# Revit family: Hager-Volta-IP30-Surface_mounted-empty-NoHosted-PL-en
name_source: partatom
category: Electrical Equipment
units: mm (PartAtom-declared; Revit-internal decimal feet)

## family parameters
Always vertical = Yes
Cut with Voids When Loaded = No
Panel Configuration = Two Columns, Circuits Across
Part Type = Panelboard
Room Calculation Point = No
Round Connector Dimension = Use Diameter
Shared = No
Work Plane-Based = Yes

## types (4) — shared parameters
Default Elevation = 1219 mm
EF000003 - Mounting method = EV000384 - Surface mounted (plaster)
EF000008 - Width = 305 mm  [stored 1.00066 ft]
EF000049 - Depth = 96 mm  [stored 0.314961 ft]
EF000116 - RAL-number = 9010
EF000118 - With mounting plate = Yes
EF001062 - EMC-version = No
EF002950 - Width in number of modular spacings = 12
EF005474 - Degree of protection (IP) = EV006410 - IP30
EF006244 - Transparent cover/door = No
EF006306 - With lock = No
EF015776 - Earthing terminal block = No
EF015777 - Neutral terminal block = No
EF015941 - Signal passing door = No
HG000002 - With door or cover = Yes
HG000003 - Range = Volta
HG000005 - Thickness = 3 mm  [stored 0.00984252 ft]
HG000006 - Flush mounted = No
HG000009 - Double swing door = No
HG000010 - Asymmetric doors = No
HG000011 - Empty rows from bottom = No
HG000017 - Distance between poles = 18 mm  [stored 0.0590551 ft]
Manufacturer = Hager
Type Comments = Volta
zero-valued in all types: EF000218 - Built-in depth, EF000332 - Built-in height, EF000846 - Built-in width, HG000001 - Number of columns, HG000007 - Number of empty columns, HG000008 - Number of empty rows

## per-type parameters (varying)
| type | EF000007 - Colour | EF000040 - Height | EF000266 - Number of rows | EF000339 - Type of cover | EF001088 - Extension possible | EF001131 - Internal depth | EF001134 - DIN-rail | EF001596 - Material housing | EF004462 - Type of closure | EF009212 - Cover model | HG000004 - Manufacturer reference | Model |
| Surface mounted IP30 W305 H515 D96.5 12 Modular spacings - VA36NWB |  | 515 mm | 0 | EV004216 - Door | Yes | 0 mm  [stored 0 ft] | No |  | EV000154 - Other | EV009916 - With notch | VA36NWB | VA36NWB |
| Surface mounted IP30 W305 H515 D96.5 12 Modular spacings - VA36NWP | EV000202 - White | 515 mm | 3 | EV004216 - Door | Yes | 92 mm | Yes | EV000154 - Other | EV000154 - Other | EV009916 - With notch | VA36NWP | VA36NWP |
| Surface mounted IP30 W305 H640 D96.5 12 Modular spacings - VA48NWB |  | 640 mm  [stored 2.09974 ft] | 0 | EV004216 - Door | Yes | 0 mm  [stored 0 ft] | No |  | EV000154 - Other | EV009916 - With notch | VA48NWB | VA48NWB |
| Surface mounted IP30 W305 H640 D96.5 12 Modular spacings - VA48NWP |  | 640 mm  [stored 2.09974 ft] | 0 |  | No | 0 mm  [stored 0 ft] | No |  |  |  | VA48NWP | VA48NWP |

note: [stored X ft] marks values corroborated as IEEE doubles in the binary element streams (Revit-internal decimal feet)

## geometry (parser evidence)
native form markers: Sweep x14
no freeform markers — native parametric forms only
